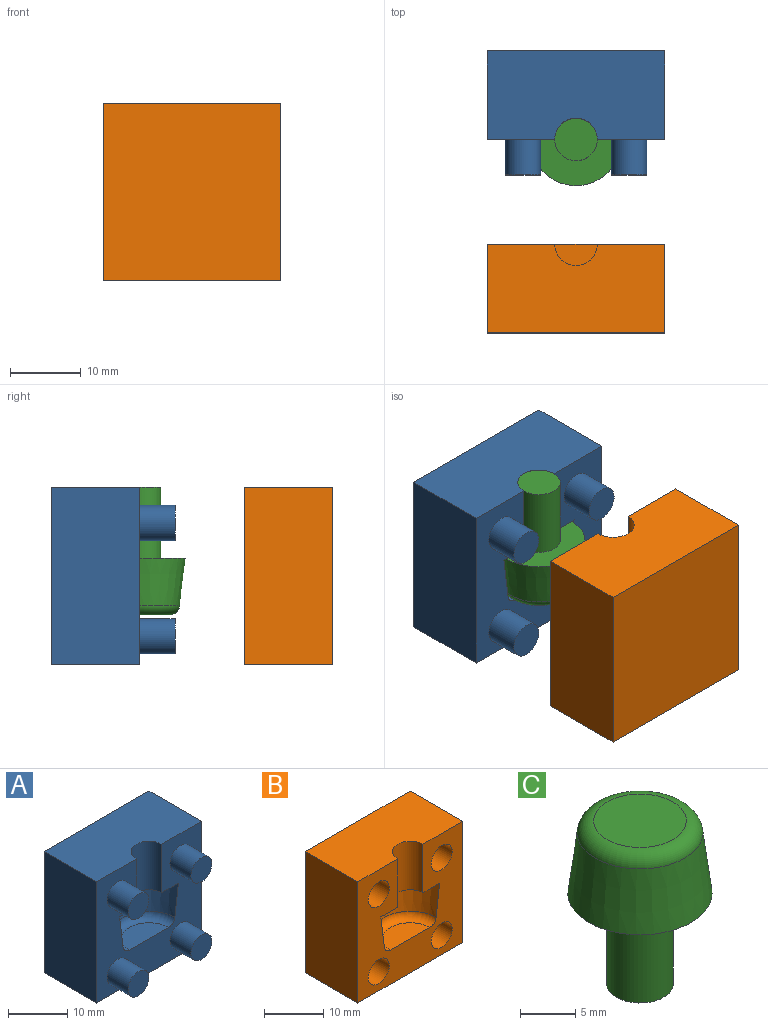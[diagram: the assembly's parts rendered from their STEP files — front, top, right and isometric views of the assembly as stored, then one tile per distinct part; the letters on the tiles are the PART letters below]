
ASSEMBLY  parts=3 mates=2
PART A: 19 faces, bbox 25x17.5x25 mm
  f0: plane 25x25mm, normal (0,-1,0), area 383.2mm2, adj f1,f2,f3,f4,f6,f7,f8,f9
  f1: plane 25x12.5mm, normal (-1,0,0), area 312.5mm2, adj f0,f2,f4,f5
  f2: plane 25x12.5mm, normal (0,0,-1), area 312.5mm2, adj f0,f1,f3,f5
  f3: plane 25x12.5mm, normal (1,0,0), area 312.5mm2, adj f0,f2,f4,f5
  f4: plane 25x12.5mm, normal (0,0,1), area 298.4mm2, adj f0,f1,f3,f5,f10
  f5: plane 25x25mm, normal (0,1,0), area 625mm2, adj f1,f2,f3,f4
  f6: plane 9.35x4.68mm, normal (0,0,1), area 34.3mm2, adj f0,f7
  f7: torus R=4.68mm, axis (0,0,-1), area 38.1mm2, adj f0,f6,f8
  f8: cone r=7mm half-angle=7.1deg, axis (0,0,1), area 139.3mm2, adj f0,f7,f9
  f9: plane 14x7mm, normal (0,0,-1), area 62.8mm2, adj f0,f8,f10
  f10: cylinder r=3mm len=10mm, axis (0,0,-1), area 94.2mm2, adj f0,f4,f9
  f11: cylinder r=2.5mm len=5mm, axis (0,1,0), area 78.5mm2, adj f0,f12
  f12: plane 5x5mm, normal (0,-1,0), area 19.6mm2, adj f11
  f13: cylinder r=2.5mm len=5mm, axis (0,1,0), area 78.5mm2, adj f0,f14
  f14: plane 5x5mm, normal (0,-1,0), area 19.6mm2, adj f13
  f15: cylinder r=2.5mm len=5mm, axis (0,1,0), area 78.5mm2, adj f0,f16
  f16: plane 5x5mm, normal (0,-1,0), area 19.6mm2, adj f15
  f17: cylinder r=2.5mm len=5mm, axis (0,1,0), area 78.5mm2, adj f0,f18
  f18: plane 5x5mm, normal (0,-1,0), area 19.6mm2, adj f17
PART B: 19 faces, bbox 25x12.5x25 mm
  f0: plane 25x25mm, normal (0,-1,0), area 383.2mm2, adj f1,f2,f3,f4,f6,f7,f8,f9
  f1: plane 25x12.5mm, normal (-1,0,0), area 312.5mm2, adj f0,f2,f4,f5
  f2: plane 25x12.5mm, normal (0,0,-1), area 312.5mm2, adj f0,f1,f3,f5
  f3: plane 25x12.5mm, normal (1,0,0), area 312.5mm2, adj f0,f2,f4,f5
  f4: plane 25x12.5mm, normal (0,0,1), area 298.4mm2, adj f0,f1,f3,f5,f10
  f5: plane 25x25mm, normal (0,1,0), area 625mm2, adj f1,f2,f3,f4
  f6: plane 9.35x4.68mm, normal (0,0,1), area 34.3mm2, adj f0,f7
  f7: torus R=4.68mm, axis (0,0,-1), area 38.1mm2, adj f0,f6,f8
  f8: cone r=7mm half-angle=7.1deg, axis (0,0,1), area 139.3mm2, adj f0,f7,f9
  f9: plane 14x7mm, normal (0,0,-1), area 62.8mm2, adj f0,f8,f10
  f10: cylinder r=3mm len=10mm, axis (0,0,-1), area 94.2mm2, adj f0,f4,f9
  f11: cylinder r=2.5mm len=5mm, axis (0,-1,0), area 78.5mm2, adj f0,f12
  f12: plane 5x5mm, normal (0,-1,0), area 19.6mm2, adj f11
  f13: cylinder r=2.5mm len=5mm, axis (0,-1,0), area 78.5mm2, adj f0,f14
  f14: plane 5x5mm, normal (0,-1,0), area 19.6mm2, adj f13
  f15: cylinder r=2.5mm len=5mm, axis (0,-1,0), area 78.5mm2, adj f0,f16
  f16: plane 5x5mm, normal (0,-1,0), area 19.6mm2, adj f15
  f17: cylinder r=2.5mm len=5mm, axis (0,-1,0), area 78.5mm2, adj f0,f18
  f18: plane 5x5mm, normal (0,-1,0), area 19.6mm2, adj f17
PART C: 6 faces, bbox 13x13x18 mm
  f0: plane 13x13mm, normal (0,0,-1), area 104.5mm2, adj f1,f4
  f1: cone r=5.66mm half-angle=7.1deg, axis (0,0,-1), area 257.5mm2, adj f0,f2
  f2: torus R=4.18mm, axis (0,0,-1), area 69.3mm2, adj f1,f3
  f3: plane 8.35x8.35mm, normal (0,0,1), area 54.8mm2, adj f2
  f4: cylinder r=3mm len=10mm, axis (0,0,1), area 188.5mm2, adj f0,f5
  f5: plane 6x6mm, normal (0,0,-1), area 28.3mm2, adj f4
PLACE A t=(2.58,21.95,2.11)mm fixed
PLACE B rot(axis=(0,0,1),180deg) t=(27.58,-17.83,2.11)mm
PLACE C rot(axis=(1,0,0),180deg) t=(15.08,9.45,17.11)mm
MATE fastened C.f1 <-> A.f7  axis (0,0,-1) through (15.08,9.45,9.11)mm
MATE slider B.f11 <-> A.f13  axis (0,1,0) through (22.58,-5.33,22.11)mm
